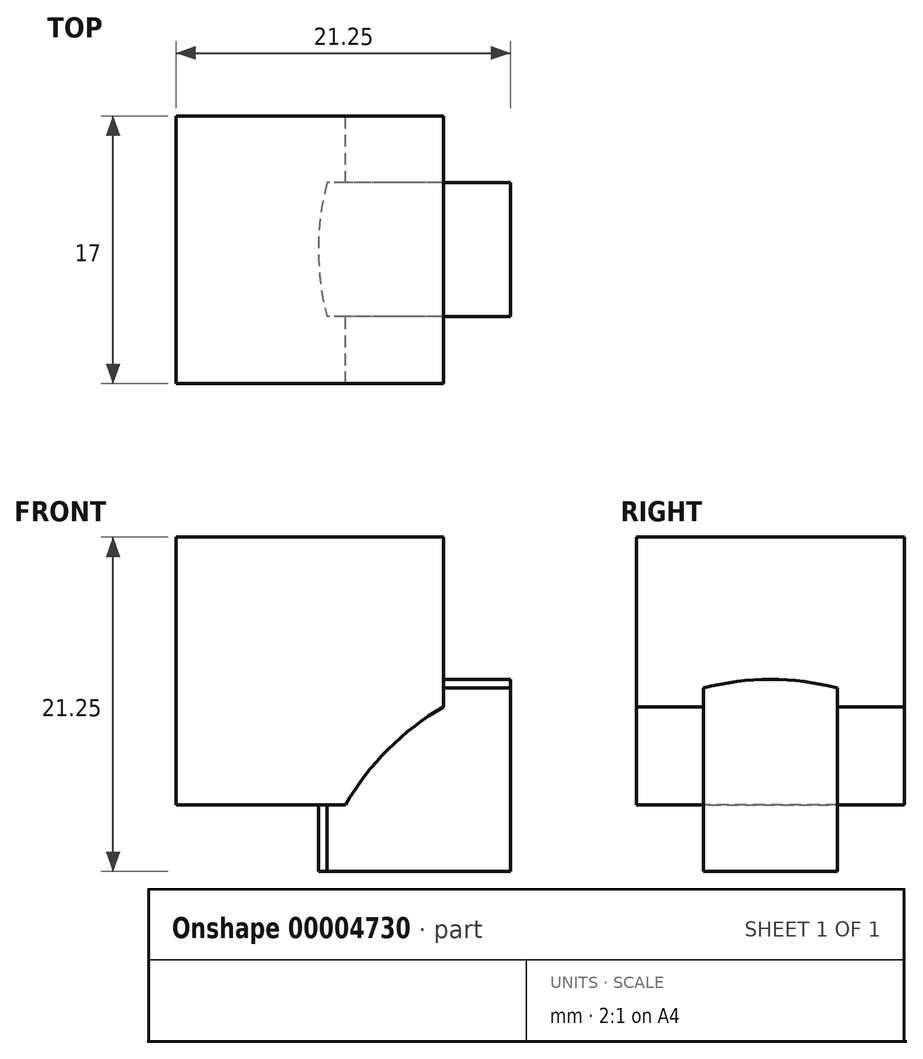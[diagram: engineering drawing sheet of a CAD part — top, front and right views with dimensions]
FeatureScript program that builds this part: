
annotation { "Feature Type Name" : "Feature", "Feature Type Description" : "" }
export const myFeature = defineFeature(function(context is Context, id is Id, definition is map)
    precondition{}
    {
        {
            var Q0;
            Q0=qCreatedBy(makeId("Front.planeOp"),FACE);
            var sketch = newSketch(context, id + "F0", { "sketchPlane" : qUnion([Q0])});
            skLineSegment(sketch, "E0.rect.bottom", {"start": v(25.5, 25.5) * mm, "end": v(-25.5, 25.5) * mm, "construction": true});
            skLineSegment(sketch, "E0.rect.top", {"start": v(25.5, -25.5) * mm, "end": v(-25.5, -25.5) * mm, "construction": true});
            skLineSegment(sketch, "E0.rect.left", {"start": v(25.5, 25.5) * mm, "end": v(25.5, -25.5) * mm, "construction": true});
            skLineSegment(sketch, "E0.rect.right", {"start": v(-25.5, 25.5) * mm, "end": v(-25.5, -25.5) * mm, "construction": true});
            skPoint(sketch, "E0.rect.middle", {"position": v(0, 0) * mm});
            skCircle(sketch, "E1", {"center": v(0, 0) * mm, "radius": 17 * mm, "construction": true});
            skLineSegment(sketch, "E2.rect.bottom", {"start": v(4.25, 8.5) * mm, "end": v(-4.25, 8.5) * mm, "construction": true});
            skLineSegment(sketch, "E2.rect.top", {"start": v(4.25, -8.5) * mm, "end": v(-4.25, -8.5) * mm, "construction": true});
            skLineSegment(sketch, "E2.rect.left", {"start": v(4.25, 8.5) * mm, "end": v(4.25, -8.5) * mm, "construction": true});
            skLineSegment(sketch, "E2.rect.right", {"start": v(-4.25, 8.5) * mm, "end": v(-4.25, -8.5) * mm, "construction": true});
            skLineSegment(sketch, "E3.rect.bottom", {"start": v(8.5, 4.25) * mm, "end": v(-8.5, 4.25) * mm, "construction": true});
            skLineSegment(sketch, "E3.rect.top", {"start": v(8.5, -4.25) * mm, "end": v(-8.5, -4.25) * mm, "construction": true});
            skLineSegment(sketch, "E3.rect.left", {"start": v(8.5, 4.25) * mm, "end": v(8.5, -4.25) * mm, "construction": true});
            skLineSegment(sketch, "E3.rect.right", {"start": v(-8.5, 4.25) * mm, "end": v(-8.5, -4.25) * mm, "construction": true});
            skSolve(sketch);
        }
        {
            var Q0;
            Q0=qCreatedBy(makeId("Front.planeOp"),FACE);
            var sketch = newSketch(context, id + "F1", { "sketchPlane" : qUnion([Q0])});
            skLineSegment(sketch, "E4.bottom", {"start": v(-4.25, 4.25) * mm, "end": v(-16.46, 4.25) * mm});
            skLineSegment(sketch, "E4.top", {"start": v(-4.25, 16.46) * mm, "end": v(-16.46, 16.46) * mm});
            skLineSegment(sketch, "E4.left", {"start": v(-4.25, 4.25) * mm, "end": v(-4.25, 16.46) * mm});
            skLineSegment(sketch, "E4.right", {"start": v(-16.46, 4.25) * mm, "end": v(-16.46, 16.46) * mm});
            skLineSegment(sketch, "E5", {"start": v(-25.5, 25.5) * mm, "end": v(-8.5, 25.5) * mm, "construction": true});
            skLineSegment(sketch, "E6", {"start": v(-8.5, 25.5) * mm, "end": v(-8.5, 0) * mm, "construction": true});
            skLineSegment(sketch, "E7", {"start": v(0, 8.5) * mm, "end": v(-25.5, 8.5) * mm, "construction": true});
            skLineSegment(sketch, "E8", {"start": v(-4.25, 14.72) * mm, "end": v(-16.46, 14.72) * mm});
            skLineSegment(sketch, "E9", {"start": v(-14.72, 4.25) * mm, "end": v(-14.72, 16.46) * mm});
            skPoint(sketch, "E10", {"position": v(-14.72, 8.5) * mm});
            skPoint(sketch, "E11", {"position": v(-8.5, 14.72) * mm});
            skPoint(sketch, "E12", {"position": v(-16.46, 8.5) * mm});
            skSolve(sketch);
        }
        {
            var Q0;
            Q0=qCreatedBy(makeId("Right.planeOp"),FACE);
            var sketch = newSketch(context, id + "F2", { "sketchPlane" : qUnion([Q0])});
            skLineSegment(sketch, "E13", {"start": v(-4.25, 14.72) * mm, "end": v(4.25, 14.72) * mm});
            skArc(sketch, "E14", {"start": v(4.25, 15.9) * mm, "mid": v(0, 16.46) * mm, "end": v(-4.25, 15.9) * mm});
            skLineSegment(sketch, "E15", {"start": v(-4.25, 14.72) * mm, "end": v(-4.25, 15.9) * mm});
            skLineSegment(sketch, "E16", {"start": v(4.25, 14.72) * mm, "end": v(4.25, 15.9) * mm});
            skSolve(sketch);
        }
        {
            var Q0;
            Q0=qCreatedBy(makeId("Top.planeOp"),FACE);
            var sketch = newSketch(context, id + "F3", { "sketchPlane" : qUnion([Q0])});
            skLineSegment(sketch, "E17", {"start": v(-14.72, 4.25) * mm, "end": v(-14.72, -4.25) * mm});
            skArc(sketch, "E18", {"start": v(-15.9, 4.25) * mm, "mid": v(-16.46, 0) * mm, "end": v(-15.9, -4.25) * mm});
            skLineSegment(sketch, "E19", {"start": v(-14.72, 4.25) * mm, "end": v(-15.9, 4.25) * mm});
            skLineSegment(sketch, "E20", {"start": v(-14.72, -4.25) * mm, "end": v(-15.9, -4.25) * mm});
            skSolve(sketch);
        }
        {
            var Q0;
            Q0=qCreatedBy(makeId("Front.planeOp"),FACE);
            var sketch = newSketch(context, id + "F4", { "sketchPlane" : qUnion([Q0])});
            skLineSegment(sketch, "E21.bottom", {"start": v(-25.5, 25.5) * mm, "end": v(-8.5, 25.5) * mm});
            skLineSegment(sketch, "E21.top", {"start": v(-25.5, 8.5) * mm, "end": v(-14.72, 8.5) * mm});
            skLineSegment(sketch, "E21.left", {"start": v(-25.5, 25.5) * mm, "end": v(-25.5, 8.5) * mm});
            skLineSegment(sketch, "E21.right", {"start": v(-8.5, 25.5) * mm, "end": v(-8.5, 14.72) * mm});
            skLineSegment(sketch, "E22", {"start": v(-8.5, 14.72) * mm, "end": v(-8.5, 8.5) * mm, "construction": true});
            skLineSegment(sketch, "E23", {"start": v(-14.72, 8.5) * mm, "end": v(-8.5, 8.5) * mm, "construction": true});
            skArc(sketch, "E24", {"start": v(-8.5, 14.72) * mm, "mid": v(-12.02, 12.02) * mm, "end": v(-14.72, 8.5) * mm});
            skArc(sketch, "E25", {"start": v(-14.72, 8.5) * mm, "mid": v(12.02, -12.02) * mm, "end": v(-8.5, 14.72) * mm, "construction": true});
            skSolve(sketch);
        }
        {
            var Q0;
            {var subQ3=sQuery(id+"F1.wireOp",EDGE,"E4.bottom");var subQ5=sQuery(id+"F1.wireOp",EDGE,"E4.left");var subQ7=makeQuery(id+"F1.imprint","INTERSECT",VERTEX,{"derivedFrom":[subQ3,subQ5]});Q0=makeQuery(id+"F1.imprint","IMPRINT",FACE,{"disambiguationData":[TD([[makeQuery(id+"F1.imprint","IMPRINT",EDGE,{"disambiguationData":[TD([[subQ7,-1.0]])],"derivedFrom":subQ3}),-1.0]])]});}
            var Q1;
            {var subQ3=sQuery(id+"F1.wireOp",EDGE,"E4.top");var subQ5=sQuery(id+"F1.wireOp",EDGE,"E4.right");var subQ7=makeQuery(id+"F1.imprint","INTERSECT",VERTEX,{"derivedFrom":[subQ3,subQ5]});Q1=makeQuery(id+"F1.imprint","IMPRINT",FACE,{"disambiguationData":[TD([[makeQuery(id+"F1.imprint","IMPRINT",EDGE,{"disambiguationData":[TD([[subQ7,1.0]])],"derivedFrom":subQ3}),1.0]])]});}
            extrude(context, id + "F5", {"entities" : qUnion([Q0, Q1]), "endBound" : BoundingType.SYMMETRIC, "depth" : 8.5 * mm});
        }
        {
            var Q0;
            Q0=makeQuery(id+"F2.imprint","IMPRINT",FACE,{"disambiguationData":[TD([[makeQuery(id+"F2.imprint","IMPRINT",EDGE,{"derivedFrom":sQuery(id+"F2.wireOp",EDGE,"E13")}),1.0]])]});
            extrude(context, id + "F6", {"entities" : qUnion([Q0]), "operationType" : NewBodyOperationType.ADD, "oppositeDirection" : true, "depth" : 15 * mm});
        }
        {
            var Q0;
            Q0=makeQuery(id+"F2.imprint","IMPRINT",FACE,{"disambiguationData":[TD([[makeQuery(id+"F2.imprint","IMPRINT",EDGE,{"derivedFrom":sQuery(id+"F2.wireOp",EDGE,"E13")}),1.0]])]});
            extrude(context, id + "F7", {"entities" : qUnion([Q0]), "operationType" : NewBodyOperationType.REMOVE, "oppositeDirection" : true, "depth" : 4.25 * mm});
        }
        {
            var Q0;
            Q0=makeQuery(id+"F3.imprint","IMPRINT",FACE,{"disambiguationData":[TD([[makeQuery(id+"F3.imprint","IMPRINT",EDGE,{"derivedFrom":sQuery(id+"F3.wireOp",EDGE,"E17")}),-1.0]])]});
            extrude(context, id + "F8", {"entities" : qUnion([Q0]), "operationType" : NewBodyOperationType.ADD, "depth" : 15 * mm});
        }
        {
            var Q0;
            Q0=makeQuery(id+"F3.imprint","IMPRINT",FACE,{"disambiguationData":[TD([[makeQuery(id+"F3.imprint","IMPRINT",EDGE,{"derivedFrom":sQuery(id+"F3.wireOp",EDGE,"E17")}),-1.0]])]});
            extrude(context, id + "F9", {"entities" : qUnion([Q0]), "operationType" : NewBodyOperationType.REMOVE, "depth" : 4.25 * mm});
        }
        {
            var Q0;
            Q0=makeQuery(id+"F4.imprint","IMPRINT",FACE,{"disambiguationData":[TD([[makeQuery(id+"F4.imprint","IMPRINT",EDGE,{"derivedFrom":sQuery(id+"F4.wireOp",EDGE,"E21.bottom")}),-1.0]])]});
            extrude(context, id + "F10", {"entities" : qUnion([Q0]), "operationType" : NewBodyOperationType.ADD, "endBound" : BoundingType.SYMMETRIC, "depth" : 17 * mm});
        }
    });
